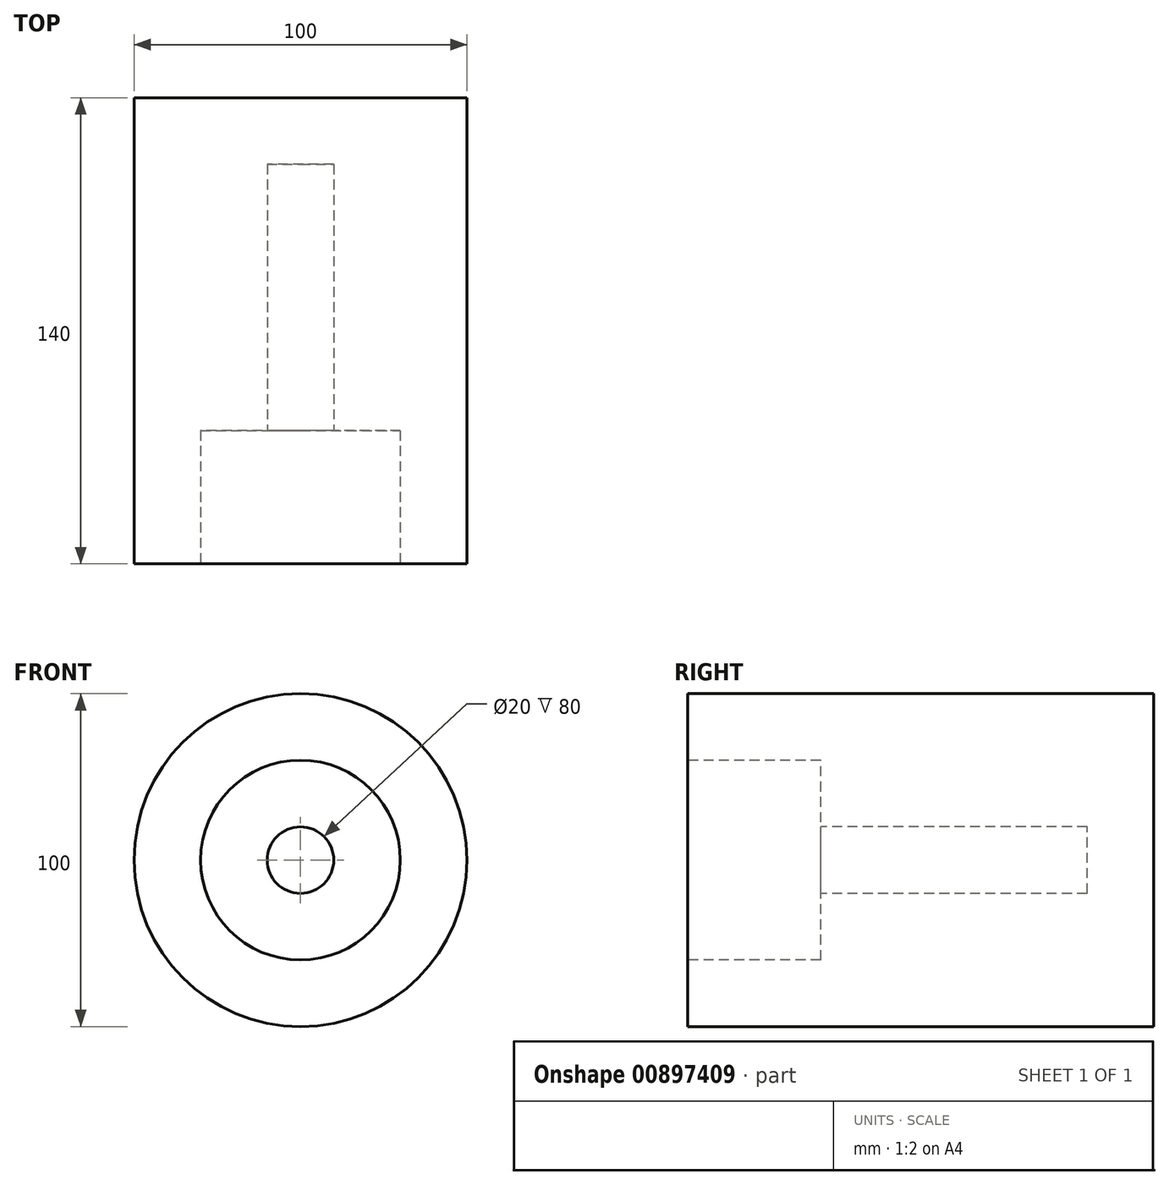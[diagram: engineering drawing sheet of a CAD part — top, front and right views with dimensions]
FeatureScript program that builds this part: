
annotation { "Feature Type Name" : "Feature", "Feature Type Description" : "" }
export const myFeature = defineFeature(function(context is Context, id is Id, definition is map)
    precondition{}
    {
        {
            var Q0;
            Q0=qCreatedBy(makeId("Front.planeOp"),FACE);
            var sketch = newSketch(context, id + "F0", { "sketchPlane" : qUnion([Q0])});
            skCircle(sketch, "E0", {"center": v(0, 0) * mm, "radius": 50 * mm});
            skSolve(sketch);
        }
        {
            var Q0;
            Q0 = qSketchRegion(id + "F0", true);
            var Q1;
            Q1=makeQuery(id+"F0.imprint","IMPRINT",FACE,{"disambiguationData":[TD([[makeQuery(id+"F0.imprint","IMPRINT",EDGE,{"derivedFrom":sQuery(id+"F0.wireOp",EDGE,"E0")}),1.0]])]});
            extrude(context, id + "F1", {"entities" : qUnion([Q0, Q1]), "depth" : 140 * mm, "offsetDistance" : 25.4 * mm});
        }
        {
            var Q0;
            Q0=makeQuery(id+"F1.opExtrude","CAP_FACE",FACE,{"disambiguationData":[OSD([sQuery(id+"F0.wireOp",EDGE,"E0")])],"isStart":false});
            var sketch = newSketch(context, id + "F2", { "sketchPlane" : qUnion([Q0])});
            skCircle(sketch, "E1", {"center": v(0, 0) * mm, "radius": 30 * mm});
            skSolve(sketch);
        }
        {
            var Q0;
            Q0=makeQuery(id+"F2.imprint","IMPRINT",FACE,{"disambiguationData":[TD([[makeQuery(id+"F2.imprint","IMPRINT",EDGE,{"derivedFrom":sQuery(id+"F2.wireOp",EDGE,"E1")}),1.0]])]});
            extrude(context, id + "F3", {"entities" : qUnion([Q0]), "operationType" : NewBodyOperationType.REMOVE, "oppositeDirection" : true, "depth" : 40 * mm, "offsetDistance" : 25.4 * mm});
        }
        {
            var Q0;
            Q0=makeQuery(id+"F3.boolean.opBoolean","COPY",FACE,{"derivedFrom":makeQuery(id+"F3.opExtrude","CAP_FACE",FACE,{"disambiguationData":[OSD([sQuery(id+"F2.wireOp",EDGE,"E1")])],"isStart":false})});
            var sketch = newSketch(context, id + "F4", { "sketchPlane" : qUnion([Q0])});
            skCircle(sketch, "E2", {"center": v(0, 0) * mm, "radius": 10 * mm});
            skSolve(sketch);
        }
        {
            var Q0;
            Q0=makeQuery(id+"F4.imprint","IMPRINT",FACE,{"disambiguationData":[TD([[makeQuery(id+"F4.imprint","IMPRINT",EDGE,{"derivedFrom":sQuery(id+"F4.wireOp",EDGE,"E2")}),1.0]])]});
            extrude(context, id + "F5", {"entities" : qUnion([Q0]), "operationType" : NewBodyOperationType.REMOVE, "oppositeDirection" : true, "depth" : 80 * mm, "offsetDistance" : 25.4 * mm});
        }
    });
